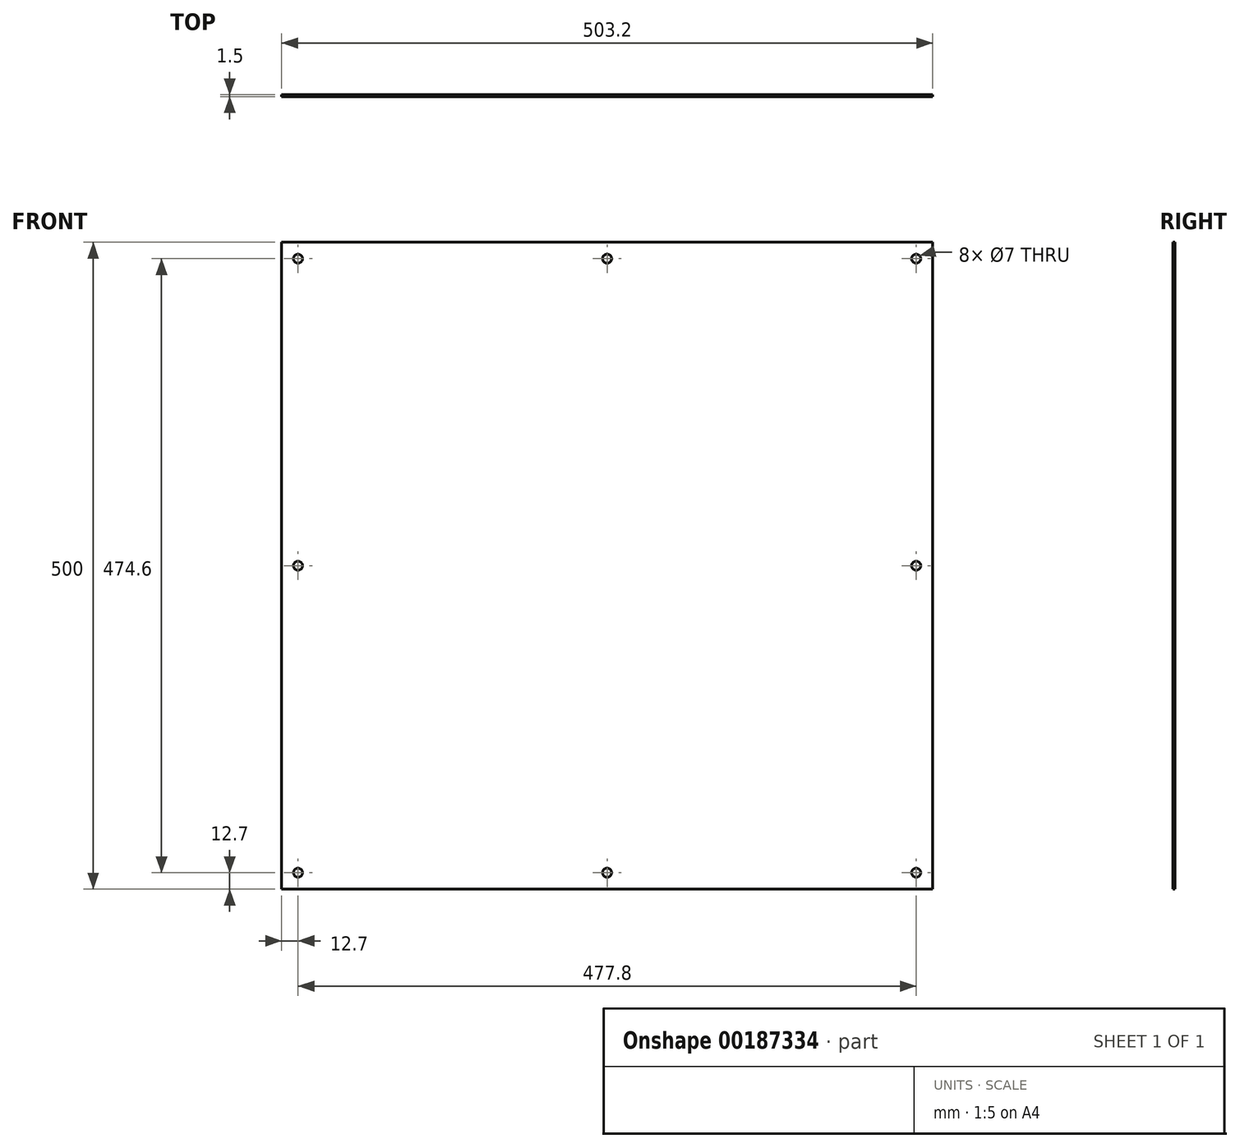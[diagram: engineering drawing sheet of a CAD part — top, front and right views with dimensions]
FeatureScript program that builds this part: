
annotation { "Feature Type Name" : "Feature", "Feature Type Description" : "" }
export const myFeature = defineFeature(function(context is Context, id is Id, definition is map)
    precondition{}
    {
        {
            var Q0;
            Q0=qCreatedBy(makeId("Front.planeOp"),FACE);
            var sketch = newSketch(context, id + "F0", { "sketchPlane" : qUnion([Q0])});
            skLineSegment(sketch, "E0.bottom", {"start": v(251.6, -250) * mm, "end": v(-251.6, -250) * mm});
            skLineSegment(sketch, "E0.top", {"start": v(251.6, 250) * mm, "end": v(-251.6, 250) * mm});
            skLineSegment(sketch, "E0.left", {"start": v(251.6, -250) * mm, "end": v(251.6, 250) * mm});
            skLineSegment(sketch, "E0.right", {"start": v(-251.6, -250) * mm, "end": v(-251.6, 250) * mm});
            skPoint(sketch, "E0.middle", {"position": v(0, 0) * mm});
            skCircle(sketch, "E1", {"center": v(-238.9, 237.3) * mm, "radius": 3.5 * mm});
            skCircle(sketch, "E2", {"center": v(238.9, 237.3) * mm, "radius": 3.5 * mm});
            skCircle(sketch, "E3", {"center": v(-238.9, -237.3) * mm, "radius": 3.5 * mm});
            skCircle(sketch, "E4", {"center": v(238.9, -237.3) * mm, "radius": 3.5 * mm});
            skCircle(sketch, "E5", {"center": v(238.9, 0) * mm, "radius": 3.5 * mm});
            skCircle(sketch, "E6", {"center": v(-238.9, 0) * mm, "radius": 3.5 * mm});
            skCircle(sketch, "E7", {"center": v(0, -237.3) * mm, "radius": 3.5 * mm});
            skCircle(sketch, "E8", {"center": v(0, 237.3) * mm, "radius": 3.5 * mm});
            skSolve(sketch);
        }
        {
            var Q0;
            Q0=qSketchRegion(id+"F0",true);
            extrude(context, id + "F1", {"entities" : qUnion([Q0]), "depth" : 1.5 * mm});
        }
    });
